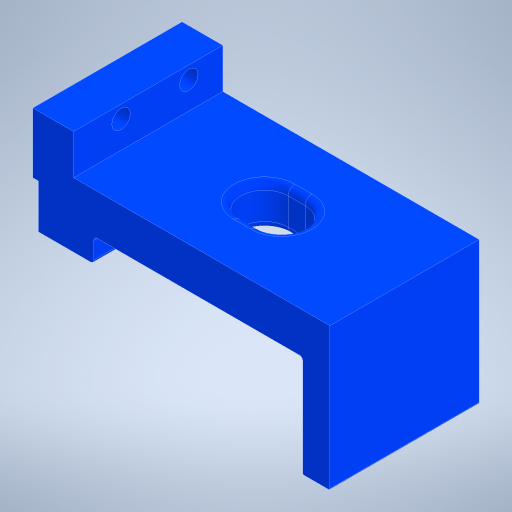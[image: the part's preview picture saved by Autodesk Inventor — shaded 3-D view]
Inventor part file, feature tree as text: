
AUTODESK INVENTOR PART (.ipt)
format: ipt  version: 2023 (Build 270158000, 158)  size: 414,208 bytes
history: native  units: in
note: dims shown in document units (in); Inventor stores cm internally (conversion verified against a paired STEP export)
features: sketch x6, extrude x3, fillet x3, other x1, hole x1
ambient origin geometry x8: Origin, YZ Plane, XZ Plane, XY Plane, X Axis, Y Axis, Z Axis, Center Point
bodies: Solid1 (feature_tree)
feature tree (14):
  other  "main_manifold_8v_v02.ipt"
  sketch  "Sketch: reference"  dims[d319=0.3in d1=1.5in]
  sketch  "Sketch: side profile"  dims[d3=0.3in d5=0.095in]
  sketch  "Sketch: MM holes"  dims[d6=0.3in d7=0.0in]
  extrude  "Ex: MM screws"  TaperAngle=0.0deg  [1 undecoded]
  hole  "Hole: MM screws (4-40)"  [1 undecoded]
  extrude  "Ex: side profile"  Depth=0.3in
  sketch  "Sketch: center hole"  dims[d8=0.135in d9=0.75in d10=0.375in d11=0.25in d12=0.5635in d13=1.0in d14=0.8108in d21=0.295in d22=0.04in d23=1.0in d24=0.0in d25=0.175in]
  extrude  "Ex: center hole"  Depth=0.295in
  fillet  "Fillet1"  Radius=0.04in
  fillet  "Fillet2"  Radius=1.0in
  fillet  "Fillet3"  Radius=0.175in
  sketch  "Sketch:MM: main inlet"  dims[d30=0.05in d34=0.47in d43=0.15in d45=0.018in d47=0.89in d48=0.085in d49=0.18in d50=0.04in d51=0.3337in d52=0.15in d53=2.125in d54=0.025in d55=0.01in d56=0.475in d58=0.175in d59=0.0in d60=0.0in d61=0.05in d62=0.125in d63=0.475in d64=0.41in d65=0.45in d67=0.2in d68=0.75in d69=0.0in d17=0.5in d18=0.0344in d19=0.5in d20=0.0344in]
  sketch  "Sketch:MM: mounting screws:1"  dims[d0=0.3937in d439=0.0in]
note: 2 required parameter values undecoded (feature->parameter linkage not recoverable at this tier; creation-order binding heuristic only, values carry confidence <= 0.55)
